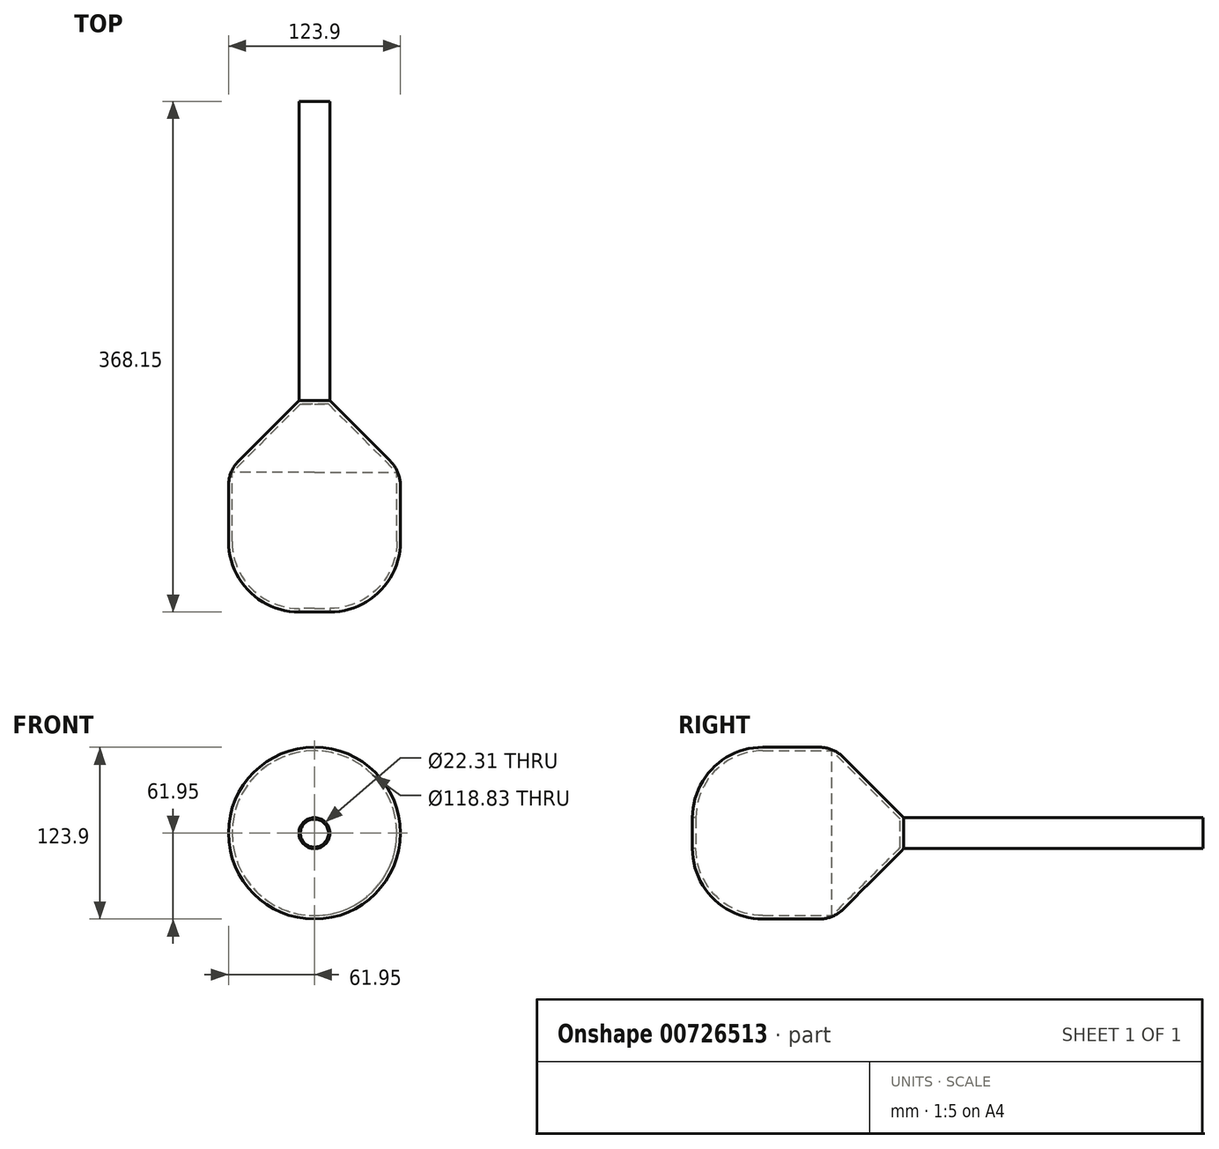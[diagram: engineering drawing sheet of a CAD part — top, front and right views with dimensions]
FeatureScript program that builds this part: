
annotation { "Feature Type Name" : "Feature", "Feature Type Description" : "" }
export const myFeature = defineFeature(function(context is Context, id is Id, definition is map)
    precondition{}
    {
        {
            var Q0;
            Q0=qCreatedBy(makeId("Front.planeOp"),FACE);
            var sketch = newSketch(context, id + "F0", { "sketchPlane" : qUnion([Q0])});
            skCircle(sketch, "E0", {"center": v(0, 0) * mm, "radius": 61.95 * mm});
            skSolve(sketch);
        }
        {
            var Q0;
            Q0=makeQuery(id+"F0.imprint","IMPRINT",FACE,{"disambiguationData":[TD([[makeQuery(id+"F0.imprint","IMPRINT",EDGE,{"derivedFrom":sQuery(id+"F0.wireOp",EDGE,"E0")}),1.0]])]});
            extrude(context, id + "F1", {"entities" : qUnion([Q0]), "depth" : 25.4 * mm, "offsetDistance" : 25.4 * mm});
        }
        {
            var Q0;
            Q0=makeQuery(id+"F1.opExtrude","CAP_FACE",FACE,{"disambiguationData":[OSD([sQuery(id+"F0.wireOp",EDGE,"E0")])],"isStart":false});
            extrude(context, id + "F2", {"entities" : qUnion([Q0]), "operationType" : NewBodyOperationType.ADD, "depth" : 127 * mm, "offsetDistance" : 25.4 * mm});
        }
        {
            var Q0;
            Q0=makeQuery(id+"F2.opExtrude","CAP_EDGE",EDGE,{"disambiguationData":[OSD([sQuery(id+"F0.wireOp",EDGE,"E0")])],"isStart":false});
            fillet(context, id + "F3", {"entities" : qUnion([Q0]), "radius" : 50.8 * mm, "tangentPropagation" : true, "allowEdgeOverflow" : false});
        }
        {
            var Q0;
            Q0=makeQuery(id+"F1.opExtrude","CAP_EDGE",EDGE,{"disambiguationData":[OSD([sQuery(id+"F0.wireOp",EDGE,"E0")])],"isStart":true});
            chamfer(context, id + "F4", {"entities" : qUnion([Q0]), "width" : 50.8 * mm, "tangentPropagation" : true});
        }
        {
            var Q0;
            Q0=makeQuery(id+"F2.opExtrude","CAP_FACE",FACE,{"disambiguationData":[OSD([sQuery(id+"F0.wireOp",EDGE,"E0")])],"isStart":false});
            shell(context, id + "F5", {"entities" : qUnion([Q0]), "thickness" : 2.54 * mm});
        }
        {
            var Q0;
            Q0=makeQuery(id+"F1.opExtrude","CAP_FACE",FACE,{"disambiguationData":[OSD([sQuery(id+"F0.wireOp",EDGE,"E0")])],"isStart":true});
            var sketch = newSketch(context, id + "F6", { "sketchPlane" : qUnion([Q0])});
            skCircle(sketch, "E1", {"center": v(0, 0) * mm, "radius": 11.7 * mm});
            skSolve(sketch);
        }
        {
            var Q0;
            Q0=qCreatedBy(makeId("Right.planeOp"),FACE);
            var sketch = newSketch(context, id + "F7", { "sketchPlane" : qUnion([Q0])});
            skLineSegment(sketch, "E2", {"start": v(215.75, 0) * mm, "end": v(0, 0) * mm});
            skSolve(sketch);
        }
        {
            var Q0;
            {var subQ0=sQuery(id+"F0.wireOp",EDGE,"E0");Q0=makeQuery(id+"F6.imprint","IMPRINT",FACE,{"disambiguationData":[TD([[makeQuery(id+"F6.imprint","IMPRINT",EDGE,{"derivedFrom":makeQuery(id+"F4.opChamfer","BLEND_EDGE",EDGE,{"blendedFrom":[makeQuery(id+"F1.opExtrude","CAP_EDGE",EDGE,{"disambiguationData":[OSD([subQ0])],"isStart":true}),makeQuery(id+"F1.opExtrude","CAP_FACE",FACE,{"disambiguationData":[OSD([subQ0])],"isStart":true})],"blendedInto":[makeQuery(id+"F1.opExtrude","CAP_FACE",FACE,{"disambiguationData":[OSD([subQ0])],"isStart":true})]})}),1.0]])]});}
            var Q1;
            Q1=sQuery(id+"F7.wireOp",EDGE,"E2");
            sweep(context, id + "F8", {"operationType" : NewBodyOperationType.ADD, "profiles" : qUnion([Q0]), "path" : qUnion([Q1])});
        }
        {
            var Q0;
            {var subQ0=sQuery(id+"F0.wireOp",EDGE,"E0");Q0=makeQuery(id+"F4.opChamfer","BLEND_EDGE",EDGE,{"blendedFrom":[makeQuery(id+"F1.opExtrude","CAP_EDGE",EDGE,{"disambiguationData":[OSD([subQ0])],"isStart":true}),makeQuery(id+"F2.boolean.opBoolean","MERGE",FACE,{"derivedFrom":[makeQuery(id+"F1.opExtrude","SWEPT_FACE",FACE,{"disambiguationData":[OSD([subQ0])]}),makeQuery(id+"F2.opExtrude","SWEPT_FACE",FACE,{"disambiguationData":[OSD([subQ0])]})]})],"blendedInto":[makeQuery(id+"F2.boolean.opBoolean","MERGE",FACE,{"derivedFrom":[makeQuery(id+"F1.opExtrude","SWEPT_FACE",FACE,{"disambiguationData":[OSD([subQ0])]}),makeQuery(id+"F2.opExtrude","SWEPT_FACE",FACE,{"disambiguationData":[OSD([subQ0])]})]})]});}
            fillet(context, id + "F9", {"entities" : qUnion([Q0]), "radius" : 25.4 * mm, "tangentPropagation" : true, "allowEdgeOverflow" : false});
        }
    });
